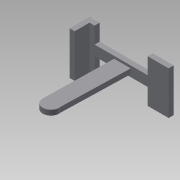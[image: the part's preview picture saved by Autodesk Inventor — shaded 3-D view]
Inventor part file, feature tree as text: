
AUTODESK INVENTOR PART (.ipt)
format: ipt  version: 2015 SP1 (Build 190203100, 203)  size: 124,928 bytes
history: native  units: mm
features: extrude x4, sketch x3, plane x2
ambient origin geometry x8: Origin, YZ Plane, XZ Plane, XY Plane, X Axis, Y Axis, Z Axis, Center Point
bodies: Solid1 (feature_tree)
feature tree (9):
  plane  "Work Plane5"
  sketch  "Sketch4"  dims[d34=15.0mm d36=2.0mm]
  extrude  "Extrusion7"  Depth=2.0mm
  extrude  "Extrusion8"  Depth=17.0mm TaperAngle=0.0deg
  plane  "Work Plane4"
  extrude  "Extrusion9"  Depth=2.0mm
  extrude  "Extrusion10"  Depth=2.0mm
  sketch  "Sketch5"  dims[d37=2.0mm d38=0.0mm d39=17.0mm d40=0.0mm]
  sketch  "Sketch6"  dims[d41=17.0mm d42=0.0mm d43=2.0mm d44=2.0mm d45=2.0mm d46=2.0mm d47=2.0mm d48=0.0mm]
